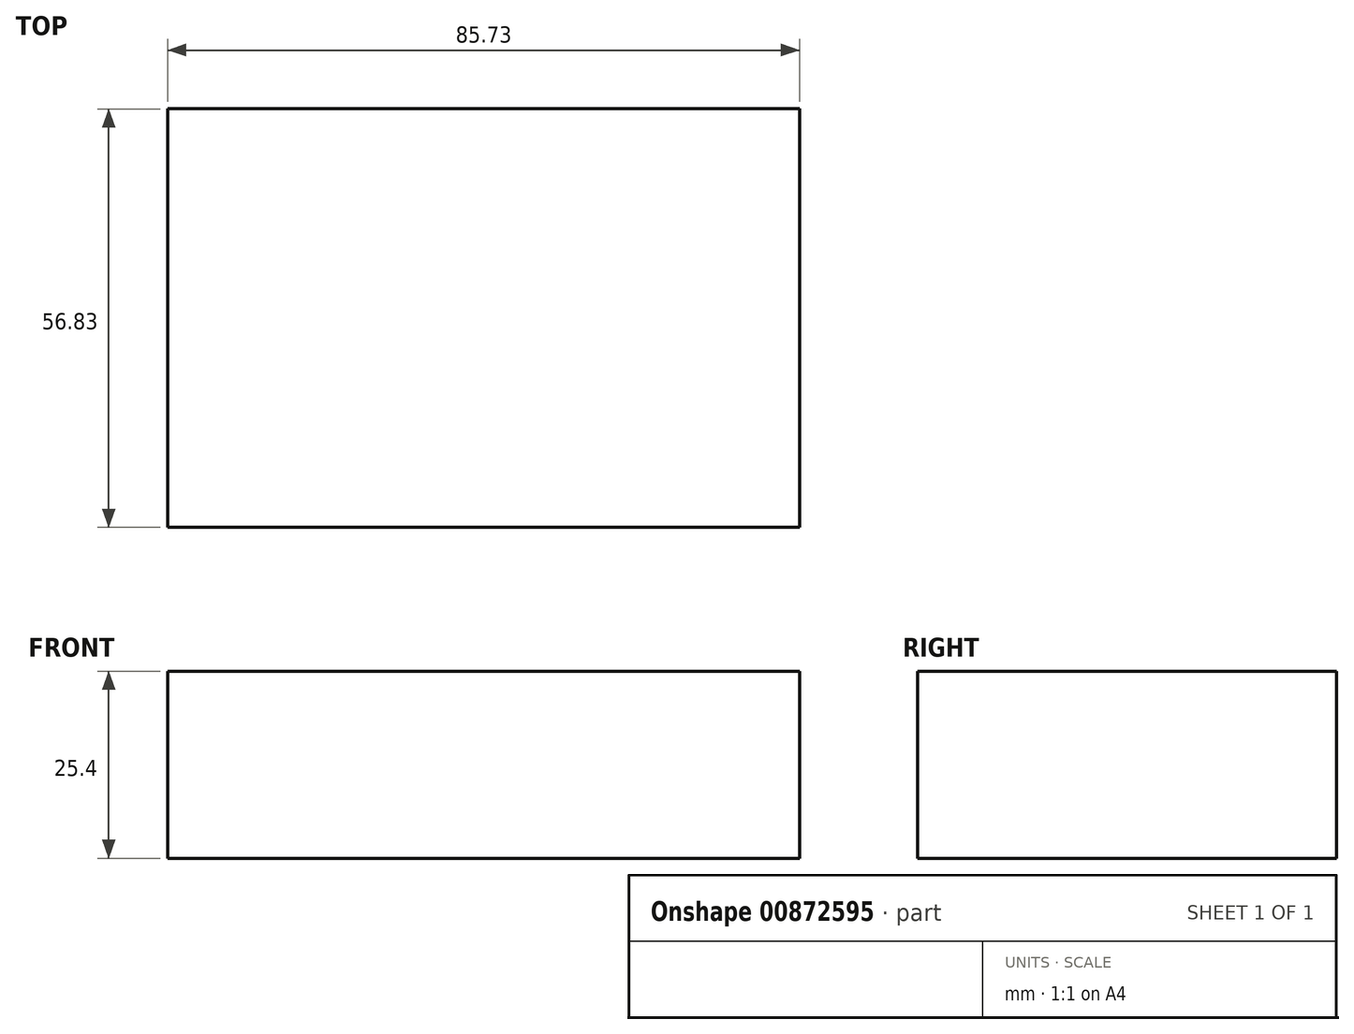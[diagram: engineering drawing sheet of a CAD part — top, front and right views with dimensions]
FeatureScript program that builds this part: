
annotation { "Feature Type Name" : "Feature", "Feature Type Description" : "" }
export const myFeature = defineFeature(function(context is Context, id is Id, definition is map)
    precondition{}
    {
        {
            var Q0;
            Q0=qCreatedBy(makeId("Top.planeOp"),FACE);
            var sketch = newSketch(context, id + "F0", { "sketchPlane" : qUnion([Q0])});
            skLineSegment(sketch, "E0.bottom", {"start": v(-38.5, 31.26) * mm, "end": v(47.23, 31.26) * mm});
            skLineSegment(sketch, "E0.top", {"start": v(-38.5, -25.57) * mm, "end": v(47.23, -25.57) * mm});
            skLineSegment(sketch, "E0.left", {"start": v(-38.5, 31.26) * mm, "end": v(-38.5, -25.57) * mm});
            skLineSegment(sketch, "E0.right", {"start": v(47.23, 31.26) * mm, "end": v(47.23, -25.57) * mm});
            skSolve(sketch);
        }
        {
            var Q0;
            Q0=makeQuery(id+"F0.imprint","IMPRINT",FACE,{"disambiguationData":[TD([[makeQuery(id+"F0.imprint","IMPRINT",EDGE,{"derivedFrom":sQuery(id+"F0.wireOp",EDGE,"E0.bottom")}),-1.0]])]});
            extrude(context, id + "F1", {"entities" : qUnion([Q0]), "depth" : 25.4 * mm, "offsetDistance" : 25.4 * mm});
        }
    });
